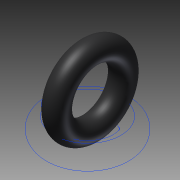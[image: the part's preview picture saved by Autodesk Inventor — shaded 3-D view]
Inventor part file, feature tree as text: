
AUTODESK INVENTOR PART (.ipt)
format: ipt  version: 2012 SP1 (Build 160190100, 190)  size: 174,592 bytes
history: native  units: in
note: dims shown in document units (in); Inventor stores cm internally (conversion verified against a paired STEP export)
features: sketch x2, sweep x1
ambient origin geometry x8: Origin, YZ Plane, XZ Plane, XY Plane, X Axis, Y Axis, Z Axis, Center Point
bodies: Solid1 (feature_tree)
feature tree (3):
  sweep  "Sweep1"
  sketch  "Sketch1"  dims[d0=0.07in d1=0.145in]
  sketch  "Sketch2"  dims[d3=0.0in]
